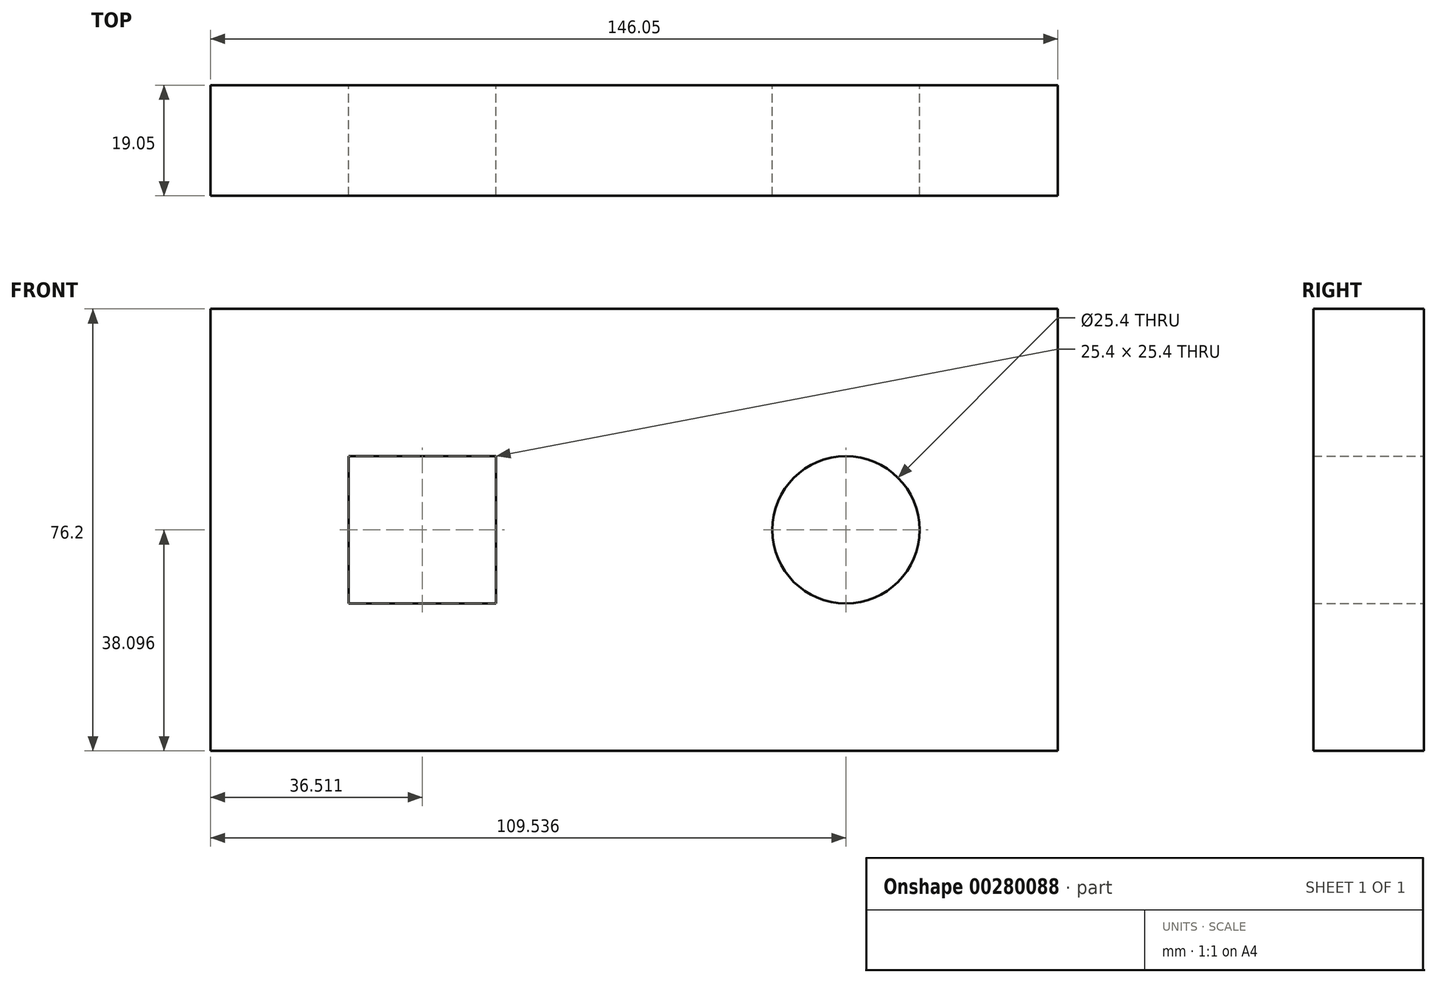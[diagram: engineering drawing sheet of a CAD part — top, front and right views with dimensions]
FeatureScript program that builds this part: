
annotation { "Feature Type Name" : "Feature", "Feature Type Description" : "" }
export const myFeature = defineFeature(function(context is Context, id is Id, definition is map)
    precondition{}
    {
        {
            var Q0;
            Q0=qCreatedBy(makeId("Front.planeOp"),FACE);
            var sketch = newSketch(context, id + "F0", { "sketchPlane" : qUnion([Q0])});
            skLineSegment(sketch, "E0.bottom", {"start": v(-89.91, 63.56) * mm, "end": v(56.14, 63.56) * mm});
            skLineSegment(sketch, "E0.top", {"start": v(-89.91, -12.64) * mm, "end": v(56.14, -12.64) * mm});
            skLineSegment(sketch, "E0.left", {"start": v(-89.91, 63.56) * mm, "end": v(-89.91, -12.64) * mm});
            skLineSegment(sketch, "E0.right", {"start": v(56.14, 63.56) * mm, "end": v(56.14, -12.64) * mm});
            skLineSegment(sketch, "E1.bottom", {"start": v(-66.1, 38.16) * mm, "end": v(-40.7, 38.16) * mm});
            skLineSegment(sketch, "E1.top", {"start": v(-66.1, 12.76) * mm, "end": v(-40.7, 12.76) * mm});
            skLineSegment(sketch, "E1.left", {"start": v(-66.1, 38.16) * mm, "end": v(-66.1, 12.76) * mm});
            skLineSegment(sketch, "E1.right", {"start": v(-40.7, 38.16) * mm, "end": v(-40.7, 12.76) * mm});
            skCircle(sketch, "E2", {"center": v(19.63, 25.46) * mm, "radius": 12.7 * mm});
            skSolve(sketch);
        }
        {
            var Q0;
            Q0 = qSketchRegion(id + "F0", true);
            extrude(context, id + "F1", {"entities" : qUnion([Q0]), "depth" : 19.05 * mm});
        }
    });
